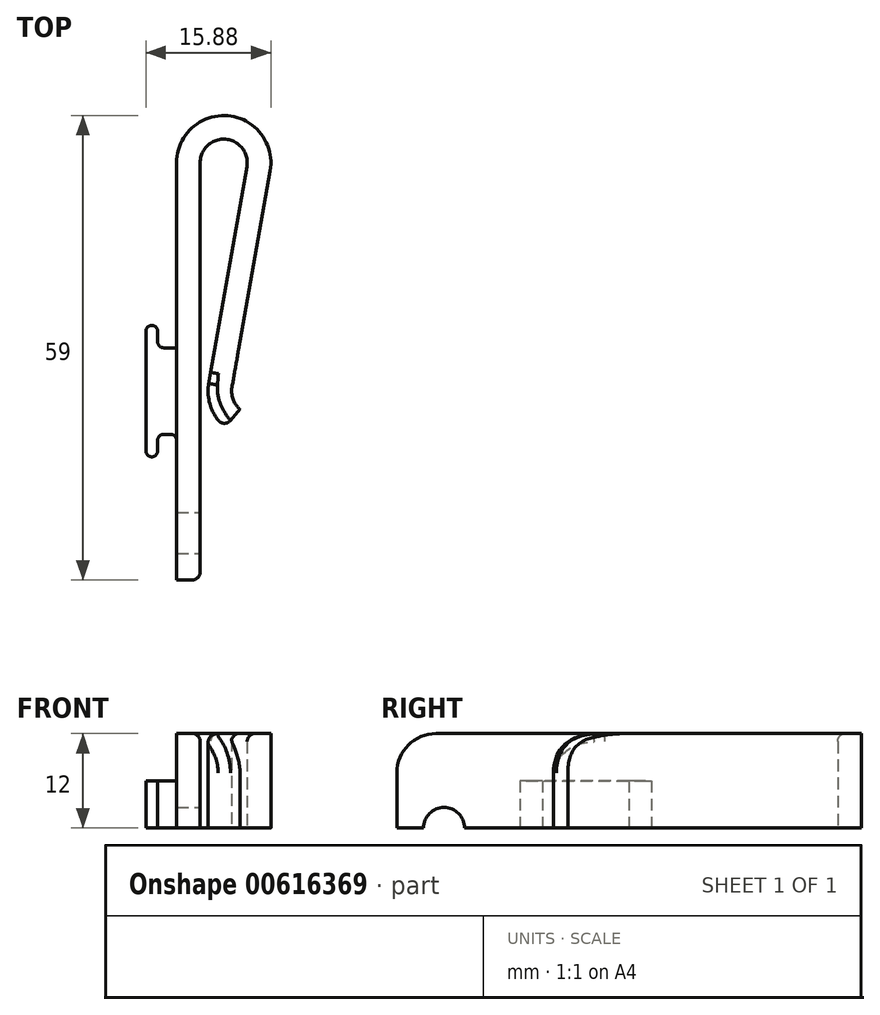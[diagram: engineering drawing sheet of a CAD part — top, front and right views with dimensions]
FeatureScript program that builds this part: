
annotation { "Feature Type Name" : "Feature", "Feature Type Description" : "" }
export const myFeature = defineFeature(function(context is Context, id is Id, definition is map)
    precondition{}
    {
        {
            var Q0;
            Q0=qCreatedBy(makeId("Top.planeOp"),FACE);
            var sketch = newSketch(context, id + "F0", { "sketchPlane" : qUnion([Q0])});
            skLineSegment(sketch, "E0", {"start": v(0, -24) * mm, "end": v(0, -5.5) * mm});
            skLineSegment(sketch, "E1", {"start": v(0, -5.5) * mm, "end": v(-2.4, -5.5) * mm});
            skLineSegment(sketch, "E2", {"start": v(-2.4, -5.5) * mm, "end": v(-2.4, -8.35) * mm});
            skLineSegment(sketch, "E3", {"start": v(-2.4, -8.35) * mm, "end": v(-3.9, -8.35) * mm});
            skLineSegment(sketch, "E4", {"start": v(-3.9, -8.35) * mm, "end": v(-3.9, 8.35) * mm});
            skLineSegment(sketch, "E5", {"start": v(-3.9, 8.35) * mm, "end": v(-2.4, 8.35) * mm});
            skLineSegment(sketch, "E6", {"start": v(-2.4, 8.35) * mm, "end": v(-2.4, 5.5) * mm});
            skLineSegment(sketch, "E7", {"start": v(-2.4, 5.5) * mm, "end": v(0, 5.5) * mm});
            skLineSegment(sketch, "E8", {"start": v(0, 5.5) * mm, "end": v(0, 29.01) * mm});
            skArc(sketch, "E9", {"start": v(11.89, 27.97) * mm, "mid": v(6.51, 34.98) * mm, "end": v(0, 29.01) * mm});
            skLineSegment(sketch, "E10", {"start": v(11.89, 27.97) * mm, "end": v(7.05, 0.52) * mm});
            skArc(sketch, "E11", {"start": v(7.05, 0.52) * mm, "mid": v(7.18, -1.02) * mm, "end": v(8.07, -2.29) * mm});
            skLineSegment(sketch, "E12", {"start": v(8.07, -2.29) * mm, "end": v(6.14, -4.59) * mm});
            skArc(sketch, "E13", {"start": v(4.1, 1.04) * mm, "mid": v(4.36, -2.05) * mm, "end": v(6.14, -4.59) * mm});
            skLineSegment(sketch, "E14", {"start": v(4.1, 1.04) * mm, "end": v(8.93, 28.5) * mm});
            skArc(sketch, "E15", {"start": v(8.93, 28.5) * mm, "mid": v(6.25, 31.99) * mm, "end": v(3, 29.01) * mm});
            skLineSegment(sketch, "E16", {"start": v(3, 29.01) * mm, "end": v(3, -24) * mm});
            skLineSegment(sketch, "E17", {"start": v(3, -24) * mm, "end": v(0, -24) * mm});
            skLineSegment(sketch, "E18", {"start": v(-3.9, 0) * mm, "end": v(0, 0) * mm, "construction": true});
            skSolve(sketch);
        }
        {
            var Q0;
            Q0=makeQuery(id+"F0.imprint","IMPRINT",FACE,{"disambiguationData":[TD([[makeQuery(id+"F0.imprint","IMPRINT",EDGE,{"derivedFrom":sQuery(id+"F0.wireOp",EDGE,"E0")}),-1.0]])]});
            extrude(context, id + "F1", {"entities" : qUnion([Q0]), "depth" : 12 * mm, "offsetDistance" : 25 * mm});
        }
        {
            var Q0;
            Q0=makeQuery(id+"F1.opExtrude","SWEPT_FACE",FACE,{"disambiguationData":[OSD([sQuery(id+"F0.wireOp",EDGE,"E16")])]});
            var sketch = newSketch(context, id + "F2", { "sketchPlane" : qUnion([Q0])});
            skCircle(sketch, "E19", {"center": v(-18, 0) * mm, "radius": 2.6 * mm});
            skSolve(sketch);
        }
        {
            var Q0;
            Q0=makeQuery(id+"F2.imprint","IMPRINT",FACE,{"disambiguationData":[TD([[makeQuery(id+"F2.imprint","IMPRINT",EDGE,{"derivedFrom":sQuery(id+"F2.wireOp",EDGE,"E19")}),1.0]])]});
            extrude(context, id + "F3", {"entities" : qUnion([Q0]), "operationType" : NewBodyOperationType.REMOVE, "endBound" : BoundingType.THROUGH_ALL, "oppositeDirection" : true, "depth" : 25 * mm, "offsetDistance" : 25 * mm});
        }
        {
            var Q0;
            Q0=makeQuery(id+"F1.opExtrude","CAP_FACE",FACE,{"disambiguationData":[OSD([sQuery(id+"F0.wireOp",EDGE,"E0"),sQuery(id+"F0.wireOp",EDGE,"E1"),sQuery(id+"F0.wireOp",EDGE,"E2"),sQuery(id+"F0.wireOp",EDGE,"E3"),sQuery(id+"F0.wireOp",EDGE,"E4"),sQuery(id+"F0.wireOp",EDGE,"E5"),sQuery(id+"F0.wireOp",EDGE,"E6"),sQuery(id+"F0.wireOp",EDGE,"E7"),sQuery(id+"F0.wireOp",EDGE,"E8"),sQuery(id+"F0.wireOp",EDGE,"E9"),sQuery(id+"F0.wireOp",EDGE,"E10"),sQuery(id+"F0.wireOp",EDGE,"E11"),sQuery(id+"F0.wireOp",EDGE,"E12"),sQuery(id+"F0.wireOp",EDGE,"E13"),sQuery(id+"F0.wireOp",EDGE,"E14"),sQuery(id+"F0.wireOp",EDGE,"E15"),sQuery(id+"F0.wireOp",EDGE,"E16"),sQuery(id+"F0.wireOp",EDGE,"E17")])],"isStart":false});
            var sketch = newSketch(context, id + "F4", { "sketchPlane" : qUnion([Q0])});
            skLineSegment(sketch, "E20", {"start": v(0, 5.5) * mm, "end": v(0, -5.5) * mm});
            skSolve(sketch);
        }
        {
            var Q0;
            Q0 = qSketchRegion(id + "F4", true);
            var Q1;
            Q1=makeQuery(id+"F4.imprint","IMPRINT",FACE,{"disambiguationData":[TD([[makeQuery(id+"F4.imprint","IMPRINT",EDGE,{"derivedFrom":sQuery(id+"F4.wireOp",EDGE,"E20")}),-1.0]])]});
            extrude(context, id + "F5", {"entities" : qUnion([Q0, Q1]), "operationType" : NewBodyOperationType.REMOVE, "oppositeDirection" : true, "depth" : 6 * mm, "offsetDistance" : 25 * mm});
        }
        {
            var Q0;
            Q0=makeQuery(id+"F1.opExtrude","CAP_EDGE",EDGE,{"disambiguationData":[OSD([sQuery(id+"F0.wireOp",EDGE,"E17")])],"isStart":false});
            var Q1;
            Q1=makeQuery(id+"F1.opExtrude","CAP_EDGE",EDGE,{"disambiguationData":[OSD([sQuery(id+"F0.wireOp",EDGE,"E12")])],"isStart":false});
            fillet(context, id + "F6", {"entities" : qUnion([Q0, Q1]), "radius" : 5 * mm, "tangentPropagation" : true, "allowEdgeOverflow" : false});
        }
        {
            var Q0;
            Q0=makeQuery(id+"F5.boolean.opBoolean","COPY",EDGE,{"derivedFrom":makeQuery(id+"F5.opExtrude","CAP_EDGE",EDGE,{"disambiguationData":[OSD([sQuery(id+"F0.wireOp",EDGE,"E4")])],"isStart":false})});
            var Q1;
            Q1=makeQuery(id+"F5.boolean.opBoolean","COPY",EDGE,{"derivedFrom":makeQuery(id+"F5.opExtrude","CAP_EDGE",EDGE,{"disambiguationData":[OSD([sQuery(id+"F0.wireOp",EDGE,"E3")])],"isStart":false})});
            var Q2;
            Q2=makeQuery(id+"F5.boolean.opBoolean","COPY",EDGE,{"derivedFrom":makeQuery(id+"F5.opExtrude","CAP_EDGE",EDGE,{"disambiguationData":[OSD([sQuery(id+"F0.wireOp",EDGE,"E2")])],"isStart":false})});
            var Q3;
            Q3=makeQuery(id+"F5.boolean.opBoolean","COPY",EDGE,{"derivedFrom":makeQuery(id+"F5.opExtrude","CAP_EDGE",EDGE,{"disambiguationData":[OSD([sQuery(id+"F0.wireOp",EDGE,"E1")])],"isStart":false})});
            var Q4;
            Q4=makeQuery(id+"F5.boolean.opBoolean","COPY",EDGE,{"derivedFrom":makeQuery(id+"F5.opExtrude","CAP_EDGE",EDGE,{"disambiguationData":[OSD([sQuery(id+"F0.wireOp",EDGE,"E7")])],"isStart":false})});
            var Q5;
            Q5=makeQuery(id+"F5.boolean.opBoolean","COPY",EDGE,{"derivedFrom":makeQuery(id+"F5.opExtrude","CAP_EDGE",EDGE,{"disambiguationData":[OSD([sQuery(id+"F0.wireOp",EDGE,"E6")])],"isStart":false})});
            var Q6;
            Q6=makeQuery(id+"F5.boolean.opBoolean","COPY",EDGE,{"derivedFrom":makeQuery(id+"F5.opExtrude","CAP_EDGE",EDGE,{"disambiguationData":[OSD([sQuery(id+"F0.wireOp",EDGE,"E5")])],"isStart":false})});
            var Q7;
            Q7=makeQuery(id+"F1.opExtrude","SWEPT_EDGE",EDGE,{"disambiguationData":[OSD([sQuery(id+"F0.wireOp",EDGE,"E3"),sQuery(id+"F0.wireOp",EDGE,"E4")])]});
            var Q8;
            Q8=makeQuery(id+"F1.opExtrude","SWEPT_EDGE",EDGE,{"disambiguationData":[OSD([sQuery(id+"F0.wireOp",EDGE,"E2"),sQuery(id+"F0.wireOp",EDGE,"E3")])]});
            var Q9;
            Q9=makeQuery(id+"F1.opExtrude","SWEPT_EDGE",EDGE,{"disambiguationData":[OSD([sQuery(id+"F0.wireOp",EDGE,"E1"),sQuery(id+"F0.wireOp",EDGE,"E2")])]});
            var Q10;
            Q10=makeQuery(id+"F1.opExtrude","SWEPT_EDGE",EDGE,{"disambiguationData":[OSD([sQuery(id+"F0.wireOp",EDGE,"E0"),sQuery(id+"F0.wireOp",EDGE,"E1")])]});
            var Q11;
            Q11=makeQuery(id+"F1.opExtrude","SWEPT_EDGE",EDGE,{"disambiguationData":[OSD([sQuery(id+"F0.wireOp",EDGE,"E4"),sQuery(id+"F0.wireOp",EDGE,"E5")])]});
            var Q12;
            Q12=makeQuery(id+"F1.opExtrude","SWEPT_EDGE",EDGE,{"disambiguationData":[OSD([sQuery(id+"F0.wireOp",EDGE,"E5"),sQuery(id+"F0.wireOp",EDGE,"E6")])]});
            var Q13;
            Q13=makeQuery(id+"F1.opExtrude","SWEPT_EDGE",EDGE,{"disambiguationData":[OSD([sQuery(id+"F0.wireOp",EDGE,"E6"),sQuery(id+"F0.wireOp",EDGE,"E7")])]});
            fillet(context, id + "F7", {"entities" : qUnion([Q0, Q1, Q2, Q3, Q4, Q5, Q6, Q7, Q8, Q9, Q10, Q11, Q12, Q13]), "radius" : 0.75 * mm, "tangentPropagation" : true, "allowEdgeOverflow" : false});
        }
        {
            var Q0;
            Q0=makeQuery(id+"F5.boolean.opBoolean","MERGE",EDGE,{"derivedFrom":[makeQuery(id+"F1.opExtrude","CAP_EDGE",EDGE,{"disambiguationData":[OSD([sQuery(id+"F0.wireOp",EDGE,"E0")])],"isStart":false}),makeQuery(id+"F1.opExtrude","CAP_EDGE",EDGE,{"disambiguationData":[OSD([sQuery(id+"F0.wireOp",EDGE,"E8")])],"isStart":false}),makeQuery(id+"F5.opExtrude","CAP_EDGE",EDGE,{"disambiguationData":[OSD([sQuery(id+"F4.wireOp",EDGE,"E20")])],"isStart":true})]});
            var Q1;
            Q1=makeQuery(id+"F1.opExtrude","CAP_EDGE",EDGE,{"disambiguationData":[OSD([sQuery(id+"F0.wireOp",EDGE,"E16")])],"isStart":false});
            fillet(context, id + "F8", {"entities" : qUnion([Q0, Q1]), "radius" : 1 * mm, "tangentPropagation" : true, "allowEdgeOverflow" : false});
        }
    });
